# Revit family: QF_Varimixer_Kodiak20table
name_source: partatom
category: Specialty Equipment
units: mm (PartAtom-declared; Revit-internal decimal feet)

## family parameters
Always vertical = Yes
Cut with Voids When Loaded = No
OmniClass Number = 23.40.40.14.14.11
OmniClass Title = Food Mixers
Part Type = Normal
Room Calculation Point = No
Round Connector Dimension = Use Diameter
Shared = No
Work Plane-Based = No

## types (7) — shared parameters
Bowl size = 20 liter
Connected with neutral = Yes
Depth = 722 mm  [stored 2.36877 ft]
Description = Planetary mixer CR20 table
Electrical connection height = 365 mm  [stored 1.19751 ft]
Height = 787 mm  [stored 2.58202 ft]
Homepage = https://varimixer.com
Ingress protection = IP44
Length = 585 mm
Manufacturer = Varimixer A/S
Model = CR20 table
Number of phases = 1
Panel name = Kodiak
Plug included = Yes
Product description = Planetary mixer, heavy duty for whipping, kneading and mixing. 
Ergonomic - no heavy lifting
Product name = Kodiak 20 table model
URL = www.varimixer.com
URL datasheet = https://varimixer.com
Weight in Pounds = 159
Weight in kilograms = 72

## per-type parameters (varying)
| type | Cycle | Full load current | Horsepower | Power | Voltage |
| 115V/60Hz/1Ph/USA | 60 Hz | 10 A | 1.6 hp | 700 W | 115 V |
| 200V/60Hz/1Ph/Japan | 60 Hz | 6 A |  | 1500 W | 200 V |
| 200V/50Hz/1Ph/Japan | 50 Hz | 6 A |  | 1500 W | 200 V |
| 208V/60Hz/1Ph/USA | 60 Hz | 6 A | 1.6 hp | 1500 W | 208 V |
| 230V/60Hz/1Ph/USA | 60 Hz | 5 A | 1.6 hp | 700 W | 230 V |
| 230V/50Hz/1Ph/Europe | 50 Hz | 5 A |  | 700 W | 230 V |
| Others on Request | 0 Hz | 0 A |  | 0 W | 0 V |

note: [stored X ft] marks values corroborated as IEEE doubles in the binary element streams (Revit-internal decimal feet)

## geometry (parser evidence)
native form markers: Blend x10, Sweep x4
no freeform markers — native parametric forms only
